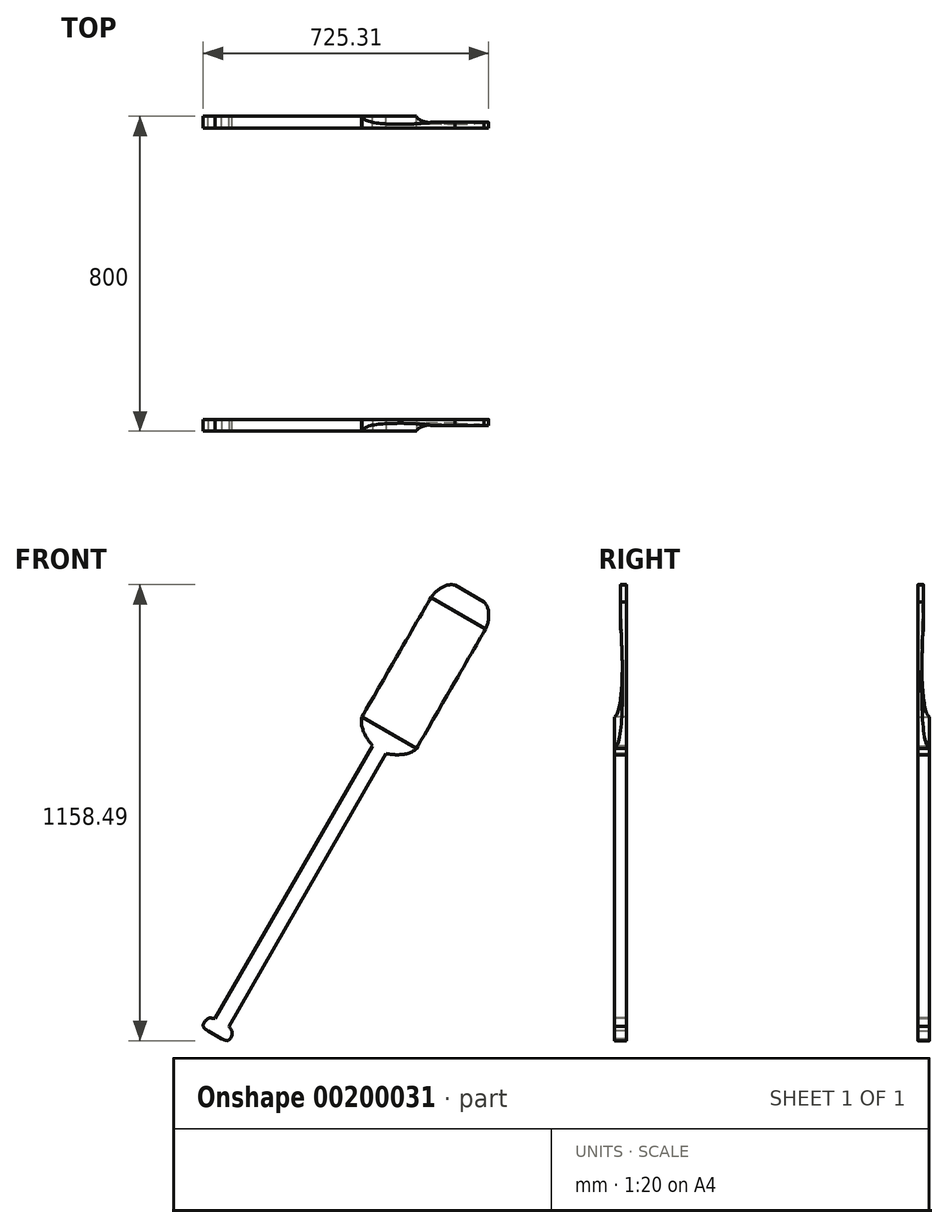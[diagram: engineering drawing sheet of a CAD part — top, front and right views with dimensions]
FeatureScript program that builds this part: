
annotation { "Feature Type Name" : "Feature", "Feature Type Description" : "" }
export const myFeature = defineFeature(function(context is Context, id is Id, definition is map)
    precondition{}
    {
        {
            var Q0;
            Q0=qCreatedBy(makeId("Front.planeOp"),FACE);
            var sketch = newSketch(context, id + "F0", { "sketchPlane" : qUnion([Q0])});
            skLineSegment(sketch, "E0", {"start": v(0, -70) * mm, "end": v(-2, -70) * mm});
            skFitSpline(sketch, "E1", {"points": [v(-2, -70) * mm, v(-3.79, -69.3) * mm, v(-3.5, -67.16) * mm, v(-2, -66.3) * mm], "startDerivative": vector(-10.04, 1.42) * mm, "endDerivative": vector(5.28, 3.14) * mm});
            skLineSegment(sketch, "E2", {"start": v(-2, -66.3) * mm, "end": v(-2, 13.7) * mm});
            skFitSpline(sketch, "E3", {"points": [v(-2, 13.7) * mm, v(-5.51, 15.46) * mm, v(-8, 18.71) * mm], "startDerivative": vector(-7.7, 2.73) * mm, "endDerivative": vector(-2.37, 8.65) * mm});
            skLineSegment(sketch, "E4", {"start": v(-8, 18.71) * mm, "end": v(-8, 53.71) * mm});
            skFitSpline(sketch, "E5", {"points": [v(-8, 53.71) * mm, v(-6.89, 57.26) * mm, v(-4.28, 59.5) * mm], "startDerivative": vector(0.08, 8) * mm, "endDerivative": vector(9.1, 3.1) * mm});
            skLineSegment(sketch, "E6", {"start": v(-4.28, 59.5) * mm, "end": v(0, 59.5) * mm});
            skLineSegment(sketch, "E7", {"start": v(0, 49.93) * mm, "end": v(0, -25.07) * mm, "construction": true});
            skLineSegment(sketch, "E8.MirrorCS", {"start": v(4.28, 59.5) * mm, "end": v(0, 59.5) * mm});
            skFitSpline(sketch, "E9.MirrorCS", {"points": [v(8, 53.71) * mm, v(6.89, 57.26) * mm, v(4.28, 59.5) * mm], "startDerivative": vector(-0.08, 8) * mm, "endDerivative": vector(-9.1, 3.1) * mm});
            skLineSegment(sketch, "E10.MirrorCS", {"start": v(8, 18.71) * mm, "end": v(8, 53.71) * mm});
            skFitSpline(sketch, "E11.MirrorCS", {"points": [v(2, 13.7) * mm, v(5.51, 15.46) * mm, v(8, 18.71) * mm], "startDerivative": vector(7.7, 2.73) * mm, "endDerivative": vector(2.37, 8.65) * mm});
            skLineSegment(sketch, "E12.MirrorCS", {"start": v(2, -66.3) * mm, "end": v(2, 13.7) * mm});
            skFitSpline(sketch, "E13.MirrorCS", {"points": [v(2, -70) * mm, v(3.79, -69.3) * mm, v(3.5, -67.16) * mm, v(2, -66.3) * mm], "startDerivative": vector(10.04, 1.42) * mm, "endDerivative": vector(-5.28, 3.14) * mm});
            skLineSegment(sketch, "E14.MirrorCS", {"start": v(0, -70) * mm, "end": v(2, -70) * mm});
            skSolve(sketch);
        }
        {
            var Q0;
            Q0=makeQuery(id+"F0.imprint","IMPRINT",FACE,{"disambiguationData":[TD([[makeQuery(id+"F0.imprint","IMPRINT",EDGE,{"derivedFrom":sQuery(id+"F0.wireOp",EDGE,"E0")}),-1.0]])]});
            extrude(context, id + "F1", {"entities" : qUnion([Q0]), "depth" : 3 * mm});
        }
        {
            var Q0;
            Q0=makeQuery(id+"F1.opExtrude","SWEPT_FACE",FACE,{"disambiguationData":[OSD([sQuery(id+"F0.wireOp",EDGE,"E10.MirrorCS")])]});
            var sketch = newSketch(context, id + "F2", { "sketchPlane" : qUnion([Q0])});
            skLineSegment(sketch, "E15", {"start": v(0, 18.71) * mm, "end": v(-1.5, 53.71) * mm});
            skLineSegment(sketch, "E16", {"start": v(-1.5, 53.71) * mm, "end": v(0, 53.71) * mm});
            skLineSegment(sketch, "E17", {"start": v(0, 53.71) * mm, "end": v(0, 18.71) * mm});
            skSolve(sketch);
        }
        {
            var Q0;
            Q0=makeQuery(id+"F2.imprint","IMPRINT",FACE,{"disambiguationData":[TD([[makeQuery(id+"F2.imprint","IMPRINT",EDGE,{"derivedFrom":sQuery(id+"F2.wireOp",EDGE,"E15")}),-1.0]])]});
            extrude(context, id + "F3", {"entities" : qUnion([Q0]), "operationType" : NewBodyOperationType.REMOVE, "oppositeDirection" : true, "depth" : 25 * mm});
        }
        {
            var Q0;
            Q0=makeQuery(id+"F3.boolean.opBoolean","COPY",FACE,{"derivedFrom":makeQuery(id+"F3.opExtrude","SWEPT_FACE",FACE,{"disambiguationData":[OSD([sQuery(id+"F2.wireOp",EDGE,"E16")])]})});
            extrude(context, id + "F4", {"entities" : qUnion([Q0]), "operationType" : NewBodyOperationType.REMOVE, "oppositeDirection" : true, "depth" : 25 * mm});
        }
        {
            var Q0;
            Q0=makeQuery(id+"F1.opExtrude","SWEPT_FACE",FACE,{"disambiguationData":[OSD([sQuery(id+"F0.wireOp",EDGE,"E10.MirrorCS")])]});
            var sketch = newSketch(context, id + "F5", { "sketchPlane" : qUnion([Q0])});
            skFitSpline(sketch, "E18", {"points": [v(0, 18.71) * mm, v(-1.98, 34.2) * mm, v(-1.93, 44.43) * mm, v(-1.75, 50.84) * mm, v(-1.5, 53.71) * mm], "startDerivative": vector(-14.57, 9.97) * mm, "endDerivative": vector(5.15, 16.62) * mm});
            skLineSegment(sketch, "E19", {"start": v(-1.5, 53.71) * mm, "end": v(0, 18.71) * mm});
            skSolve(sketch);
        }
        {
            var Q0;
            Q0=makeQuery(id+"F5.imprint","IMPRINT",FACE,{"disambiguationData":[TD([[makeQuery(id+"F5.imprint","IMPRINT",EDGE,{"derivedFrom":sQuery(id+"F5.wireOp",EDGE,"E18")}),-1.0]])]});
            extrude(context, id + "F6", {"entities" : qUnion([Q0]), "operationType" : NewBodyOperationType.REMOVE, "oppositeDirection" : true, "depth" : 25 * mm});
        }
        {
            var Q0;
            Q0=makeQuery(id+"F1.opExtrude","SWEPT_BODY",BODY,{"disambiguationData":[OSD([sQuery(id+"F0.wireOp",EDGE,"E0"),sQuery(id+"F0.wireOp",EDGE,"E1"),sQuery(id+"F0.wireOp",EDGE,"E2"),sQuery(id+"F0.wireOp",EDGE,"E3"),sQuery(id+"F0.wireOp",EDGE,"E4"),sQuery(id+"F0.wireOp",EDGE,"E5"),sQuery(id+"F0.wireOp",EDGE,"E6"),sQuery(id+"F0.wireOp",EDGE,"E8.MirrorCS"),sQuery(id+"F0.wireOp",EDGE,"E9.MirrorCS"),sQuery(id+"F0.wireOp",EDGE,"E10.MirrorCS"),sQuery(id+"F0.wireOp",EDGE,"E11.MirrorCS"),sQuery(id+"F0.wireOp",EDGE,"E12.MirrorCS"),sQuery(id+"F0.wireOp",EDGE,"E13.MirrorCS"),sQuery(id+"F0.wireOp",EDGE,"E14.MirrorCS")])]});
            var Q1;
            Q1=qCreatedBy(makeId("Origin.pointOp"),VERTEX);
            var Q2;
            Q2=qCreatedBy(makeId("Origin.pointOp"),VERTEX);
            transform(context, id + "F7", {"entities" : qUnion([Q0]), "transformType" : TransformType.SCALE_UNIFORMLY, "scale" : 10, "scalePoint" : qUnion([Q2]), "makeCopy" : false});
        }
        {
            var Q0;
            Q0=qCreatedBy(makeId("Front.planeOp"),FACE);
            cPlane(context, id + "F8", {"entities" : qUnion([Q0]), "cplaneType" : CPlaneType.OFFSET, "offset" : 400 * mm, "width" : 150 * mm, "height" : 150 * mm});
        }
        {
            var Q0;
            Q0=makeQuery(id+"F1.opExtrude","SWEPT_BODY",BODY,{"disambiguationData":[OSD([sQuery(id+"F0.wireOp",EDGE,"E0"),sQuery(id+"F0.wireOp",EDGE,"E1"),sQuery(id+"F0.wireOp",EDGE,"E2"),sQuery(id+"F0.wireOp",EDGE,"E3"),sQuery(id+"F0.wireOp",EDGE,"E4"),sQuery(id+"F0.wireOp",EDGE,"E5"),sQuery(id+"F0.wireOp",EDGE,"E6"),sQuery(id+"F0.wireOp",EDGE,"E8.MirrorCS"),sQuery(id+"F0.wireOp",EDGE,"E9.MirrorCS"),sQuery(id+"F0.wireOp",EDGE,"E10.MirrorCS"),sQuery(id+"F0.wireOp",EDGE,"E11.MirrorCS"),sQuery(id+"F0.wireOp",EDGE,"E12.MirrorCS"),sQuery(id+"F0.wireOp",EDGE,"E13.MirrorCS"),sQuery(id+"F0.wireOp",EDGE,"E14.MirrorCS")])]});
            var Q1;
            Q1=qCreatedBy(id+"F8.planeOp",FACE);
            mirror(context, id + "F9", {"entities" : qUnion([Q0]), "mirrorPlane" : qUnion([Q1])});
        }
        {
            var Q0;
            Q0=makeQuery(id+"F1.opExtrude","SWEPT_FACE",FACE,{"disambiguationData":[OSD([sQuery(id+"F0.wireOp",EDGE,"E12.MirrorCS")])]});
            var sketch = newSketch(context, id + "F10", { "sketchPlane" : qUnion([Q0])});
            skLineSegment(sketch, "E20", {"start": v(-30, -400) * mm, "end": v(0, -400) * mm, "construction": true});
            skPoint(sketch, "E21", {"position": v(-15, -400) * mm});
            skLineSegment(sketch, "E22.MirrorCS", {"start": v(-770, -400) * mm, "end": v(-800, -400) * mm, "construction": true});
            skPoint(sketch, "E23.MirrorP", {"position": v(-785, -400) * mm});
            skSolve(sketch);
        }
        {
            var Q0;
            Q0=makeQuery(id+"F1.opExtrude","SWEPT_BODY",BODY,{"disambiguationData":[OSD([sQuery(id+"F0.wireOp",EDGE,"E0"),sQuery(id+"F0.wireOp",EDGE,"E1"),sQuery(id+"F0.wireOp",EDGE,"E2"),sQuery(id+"F0.wireOp",EDGE,"E3"),sQuery(id+"F0.wireOp",EDGE,"E4"),sQuery(id+"F0.wireOp",EDGE,"E5"),sQuery(id+"F0.wireOp",EDGE,"E6"),sQuery(id+"F0.wireOp",EDGE,"E8.MirrorCS"),sQuery(id+"F0.wireOp",EDGE,"E9.MirrorCS"),sQuery(id+"F0.wireOp",EDGE,"E10.MirrorCS"),sQuery(id+"F0.wireOp",EDGE,"E11.MirrorCS"),sQuery(id+"F0.wireOp",EDGE,"E12.MirrorCS"),sQuery(id+"F0.wireOp",EDGE,"E13.MirrorCS"),sQuery(id+"F0.wireOp",EDGE,"E14.MirrorCS")])]});
            var Q1;
            Q1=makeQuery(id+"F9.opPattern","COPY",BODY,{"derivedFrom":makeQuery(id+"F1.opExtrude","SWEPT_BODY",BODY,{"disambiguationData":[OSD([sQuery(id+"F0.wireOp",EDGE,"E0"),sQuery(id+"F0.wireOp",EDGE,"E1"),sQuery(id+"F0.wireOp",EDGE,"E2"),sQuery(id+"F0.wireOp",EDGE,"E3"),sQuery(id+"F0.wireOp",EDGE,"E4"),sQuery(id+"F0.wireOp",EDGE,"E5"),sQuery(id+"F0.wireOp",EDGE,"E6"),sQuery(id+"F0.wireOp",EDGE,"E8.MirrorCS"),sQuery(id+"F0.wireOp",EDGE,"E9.MirrorCS"),sQuery(id+"F0.wireOp",EDGE,"E10.MirrorCS"),sQuery(id+"F0.wireOp",EDGE,"E11.MirrorCS"),sQuery(id+"F0.wireOp",EDGE,"E12.MirrorCS"),sQuery(id+"F0.wireOp",EDGE,"E13.MirrorCS"),sQuery(id+"F0.wireOp",EDGE,"E14.MirrorCS")])]}),"instanceName":"1"});
            var Q2;
            Q2=sQuery(id+"F10.wireOp",EDGE,"E20");
            transform(context, id + "F11", {"entities" : qUnion([Q0, Q1]), "transformType" : TransformType.ROTATION, "transformAxis" : qUnion([Q2]), "angle" : 30 * degree, "makeCopy" : false});
        }
    });
